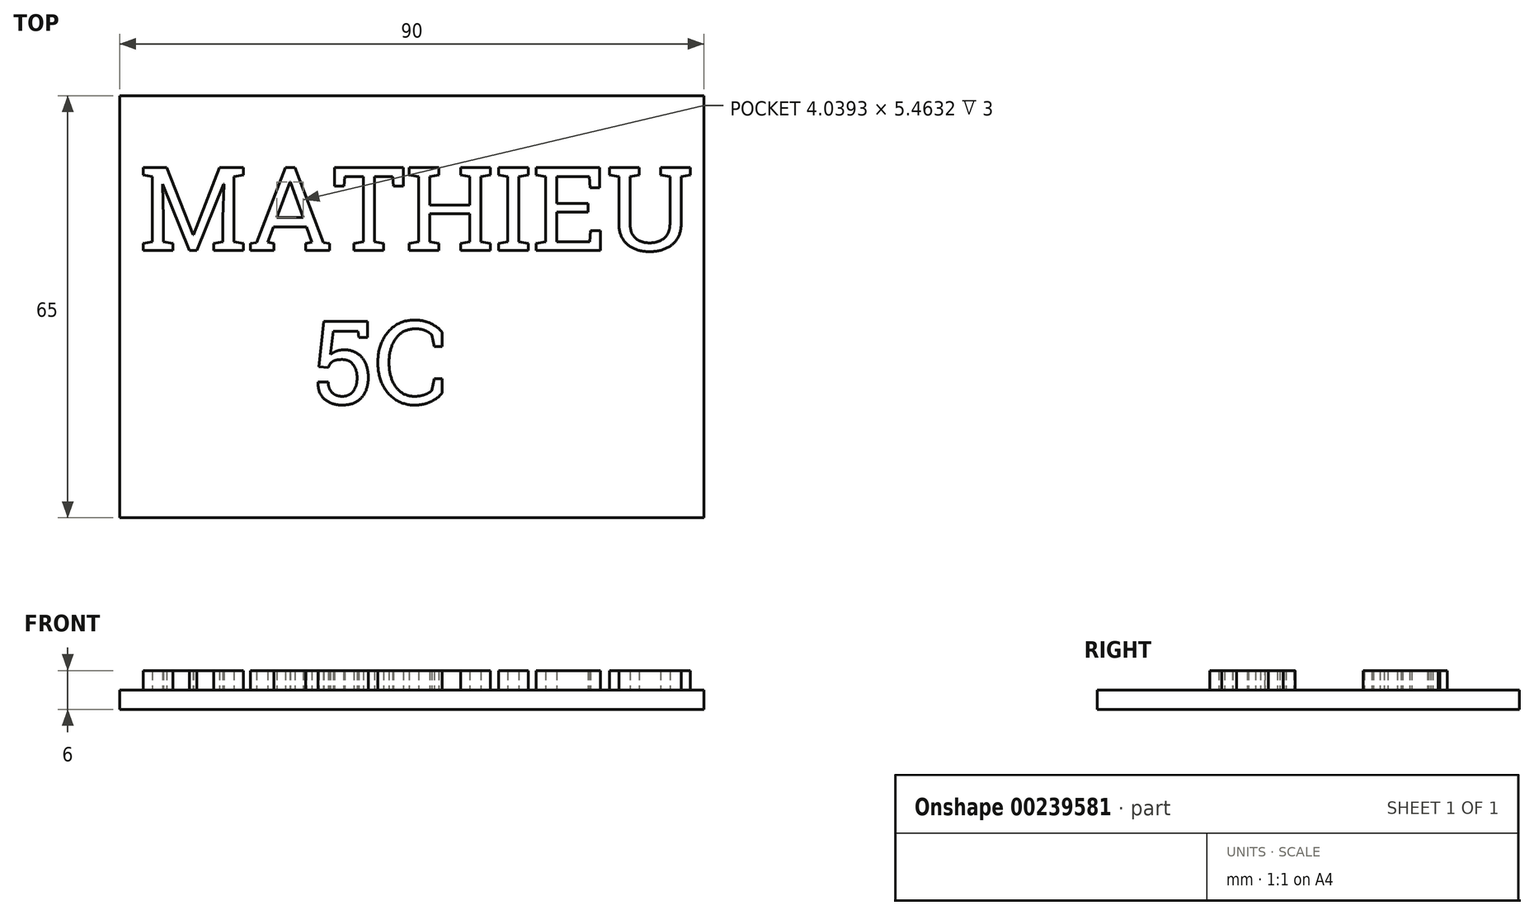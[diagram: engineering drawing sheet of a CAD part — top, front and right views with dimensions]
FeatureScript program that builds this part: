
annotation { "Feature Type Name" : "Feature", "Feature Type Description" : "" }
export const myFeature = defineFeature(function(context is Context, id is Id, definition is map)
    precondition{}
    {
        {
            var Q0;
            Q0=qCreatedBy(makeId("Top.planeOp"),FACE);
            var sketch = newSketch(context, id + "F0", { "sketchPlane" : qUnion([Q0])});
            skLineSegment(sketch, "E0.bottom", {"start": v(0, 0) * mm, "end": v(90, 0) * mm});
            skLineSegment(sketch, "E0.top", {"start": v(0, -65) * mm, "end": v(90, -65) * mm});
            skLineSegment(sketch, "E0.left", {"start": v(0, 0) * mm, "end": v(0, -65) * mm});
            skLineSegment(sketch, "E0.right", {"start": v(90, 0) * mm, "end": v(90, -65) * mm});
            skSolve(sketch);
        }
        {
            var Q0;
            Q0 = qSketchRegion(id + "F0", true);
            extrude(context, id + "F1", {"entities" : qUnion([Q0]), "depth" : 3 * mm});
        }
        {
            var Q0;
            Q0=makeQuery(id+"F1.opExtrude","CAP_FACE",FACE,{"disambiguationData":[OSD([sQuery(id+"F0.wireOp",EDGE,"E0.bottom"),sQuery(id+"F0.wireOp",EDGE,"E0.top"),sQuery(id+"F0.wireOp",EDGE,"E0.left"),sQuery(id+"F0.wireOp",EDGE,"E0.right")])],"isStart":false});
            var sketch = newSketch(context, id + "F2", { "sketchPlane" : qUnion([Q0])});
            skText(sketch, "E1", { "text": "MATHIEU \n      5C\n", "fontName": "RobotoSlab-Regular.ttf"});
            const initialGuessF2  = {"E1": [0.003, -0.02382, 1, 0, 0.01289]};
            skSetInitialGuess(sketch, initialGuessF2);
            skSolve(sketch);
        }
        {
            var Q0;
            Q0 = qSketchRegion(id + "F2", true);
            extrude(context, id + "F3", {"entities" : qUnion([Q0]), "operationType" : NewBodyOperationType.ADD, "depth" : 3 * mm});
        }
    });
